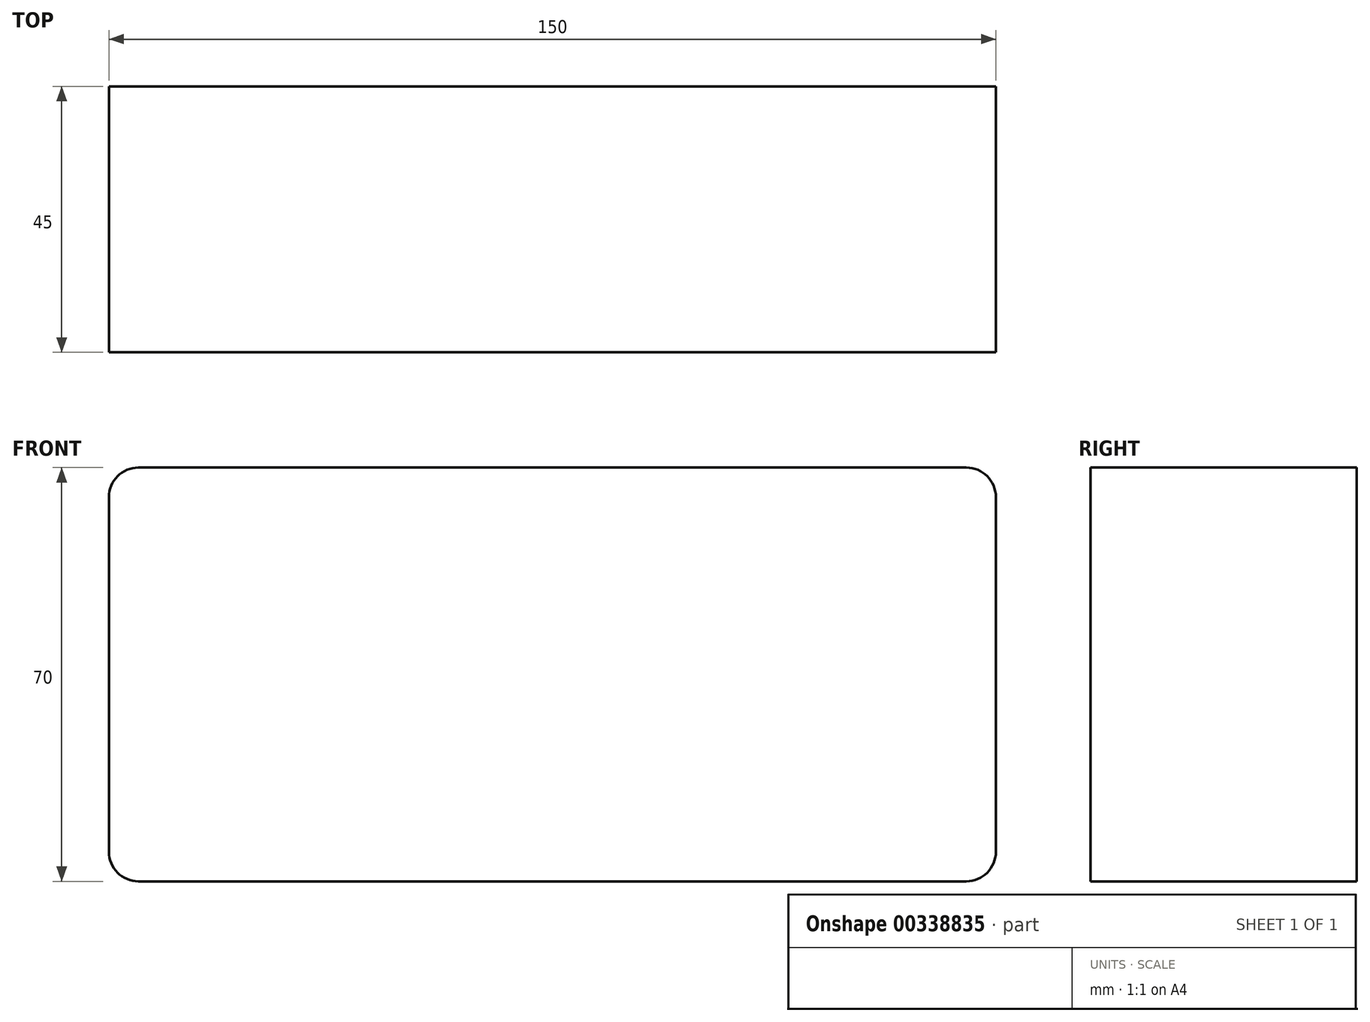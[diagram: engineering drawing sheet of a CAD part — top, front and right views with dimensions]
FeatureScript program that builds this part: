
annotation { "Feature Type Name" : "Feature", "Feature Type Description" : "" }
export const myFeature = defineFeature(function(context is Context, id is Id, definition is map)
    precondition{}
    {
        {
            var Q0;
            Q0=qCreatedBy(makeId("Right.planeOp"),FACE);
            var sketch = newSketch(context, id + "F0", { "sketchPlane" : qUnion([Q0])});
            skLineSegment(sketch, "E0.bottom", {"start": v(0, 0) * mm, "end": v(-45, 0) * mm});
            skLineSegment(sketch, "E0.top", {"start": v(0, 70) * mm, "end": v(-45, 70) * mm});
            skLineSegment(sketch, "E0.left", {"start": v(0, 0) * mm, "end": v(0, 70) * mm});
            skLineSegment(sketch, "E0.right", {"start": v(-45, 0) * mm, "end": v(-45, 70) * mm});
            skSolve(sketch);
        }
        {
            var Q0;
            Q0=makeQuery(id+"F0.imprint","IMPRINT",FACE,{"disambiguationData":[TD([[makeQuery(id+"F0.imprint","IMPRINT",EDGE,{"derivedFrom":sQuery(id+"F0.wireOp",EDGE,"E0.bottom")}),-1.0]])]});
            extrude(context, id + "F1", {"entities" : qUnion([Q0]), "depth" : 75 * mm});
        }
        {
            var Q0;
            Q0=makeQuery(id+"F1.opExtrude","SWEPT_BODY",BODY,{"disambiguationData":[OSD([sQuery(id+"F0.wireOp",EDGE,"E0.bottom"),sQuery(id+"F0.wireOp",EDGE,"E0.top"),sQuery(id+"F0.wireOp",EDGE,"E0.left"),sQuery(id+"F0.wireOp",EDGE,"E0.right")])]});
            var Q1;
            Q1=makeQuery(id+"F1.opExtrude","CAP_FACE",FACE,{"disambiguationData":[OSD([sQuery(id+"F0.wireOp",EDGE,"E0.bottom"),sQuery(id+"F0.wireOp",EDGE,"E0.top"),sQuery(id+"F0.wireOp",EDGE,"E0.left"),sQuery(id+"F0.wireOp",EDGE,"E0.right")])],"isStart":true});
            mirror(context, id + "F2", {"operationType" : NewBodyOperationType.ADD, "entities" : qUnion([Q0]), "mirrorPlane" : qUnion([Q1])});
        }
        {
            var Q0;
            Q0=makeQuery(id+"F2.opPattern","COPY",EDGE,{"derivedFrom":makeQuery(id+"F1.opExtrude","CAP_EDGE",EDGE,{"disambiguationData":[OSD([sQuery(id+"F0.wireOp",EDGE,"E0.top")])],"isStart":false}),"instanceName":"1"});
            var Q1;
            Q1=makeQuery(id+"F1.opExtrude","CAP_EDGE",EDGE,{"disambiguationData":[OSD([sQuery(id+"F0.wireOp",EDGE,"E0.top")])],"isStart":false});
            var Q2;
            Q2=makeQuery(id+"F1.opExtrude","CAP_EDGE",EDGE,{"disambiguationData":[OSD([sQuery(id+"F0.wireOp",EDGE,"E0.bottom")])],"isStart":false});
            var Q3;
            Q3=makeQuery(id+"F2.opPattern","COPY",EDGE,{"derivedFrom":makeQuery(id+"F1.opExtrude","CAP_EDGE",EDGE,{"disambiguationData":[OSD([sQuery(id+"F0.wireOp",EDGE,"E0.bottom")])],"isStart":false}),"instanceName":"1"});
            fillet(context, id + "F3", {"entities" : qUnion([Q0, Q1, Q2, Q3]), "radius" : 5 * mm, "tangentPropagation" : true, "allowEdgeOverflow" : false});
        }
    });
